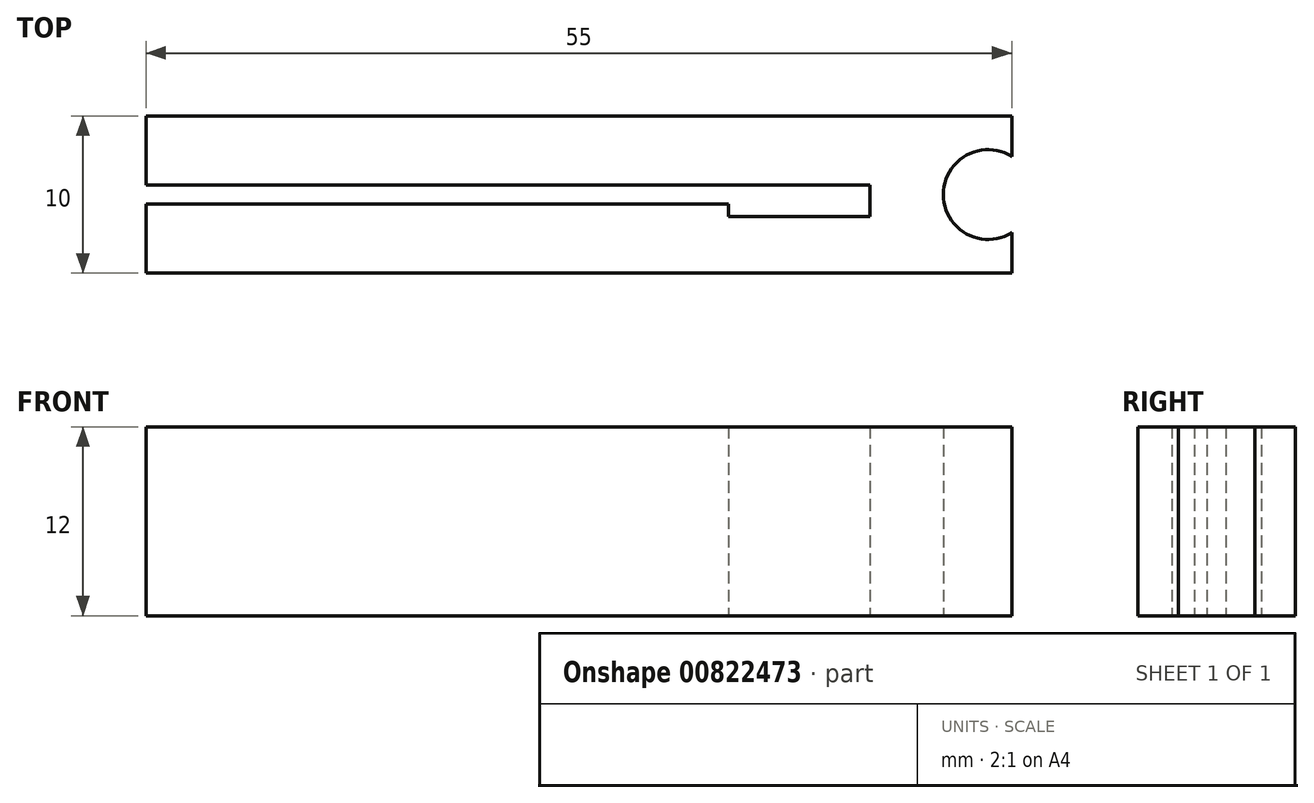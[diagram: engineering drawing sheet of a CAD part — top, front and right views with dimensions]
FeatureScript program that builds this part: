
annotation { "Feature Type Name" : "Feature", "Feature Type Description" : "" }
export const myFeature = defineFeature(function(context is Context, id is Id, definition is map)
    precondition{}
    {
        {
            var Q0;
            Q0=qCreatedBy(makeId("Top.planeOp"),FACE);
            var sketch = newSketch(context, id + "F0", { "sketchPlane" : qUnion([Q0])});
            skLineSegment(sketch, "E0.bottom", {"start": v(27.5, 5) * mm, "end": v(-27.5, 5) * mm});
            skLineSegment(sketch, "E0.top", {"start": v(27.5, -5) * mm, "end": v(-27.5, -5) * mm});
            skLineSegment(sketch, "E0.left", {"start": v(27.5, 5) * mm, "end": v(27.5, -5) * mm});
            skLineSegment(sketch, "E0.right", {"start": v(-27.5, 5) * mm, "end": v(-27.5, -5) * mm});
            skPoint(sketch, "E0.middle", {"position": v(0, 0) * mm});
            skLineSegment(sketch, "E1", {"start": v(27.5, 0) * mm, "end": v(26, 0) * mm});
            skCircle(sketch, "E2", {"center": v(26, 0) * mm, "radius": 2.85 * mm});
            skLineSegment(sketch, "E3", {"start": v(-27.5, 0) * mm, "end": v(-27.5, 0.6) * mm});
            skLineSegment(sketch, "E4", {"start": v(-27.5, 0) * mm, "end": v(-27.5, -0.6) * mm});
            skLineSegment(sketch, "E5", {"start": v(-27.5, 0.6) * mm, "end": v(18.5, 0.6) * mm});
            skLineSegment(sketch, "E6", {"start": v(18.5, 0.6) * mm, "end": v(18.5, -1.4) * mm});
            skLineSegment(sketch, "E7", {"start": v(18.5, -1.4) * mm, "end": v(9.5, -1.4) * mm});
            skLineSegment(sketch, "E8", {"start": v(9.5, -1.4) * mm, "end": v(9.5, -0.6) * mm});
            skLineSegment(sketch, "E9", {"start": v(-27.5, -0.6) * mm, "end": v(9.5, -0.6) * mm});
            skLineSegment(sketch, "E10", {"start": v(9.5, -1.4) * mm, "end": v(10.7, -1.4) * mm});
            skLineSegment(sketch, "E11", {"start": v(9.5, -0.6) * mm, "end": v(8.3, -0.6) * mm});
            skSolve(sketch);
        }
        {
            var Q0;
            {var subQ7=sQuery(id+"F0.wireOp",EDGE,"E0.bottom");Q0=makeQuery(id+"F0.imprint","IMPRINT",FACE,{"disambiguationData":[TD([[makeQuery(id+"F0.imprint","IMPRINT",EDGE,{"derivedFrom":subQ7}),1.0]])]});}
            extrude(context, id + "F1", {"entities" : qUnion([Q0]), "depth" : 12 * mm, "offsetDistance" : 25 * mm});
        }
    });
